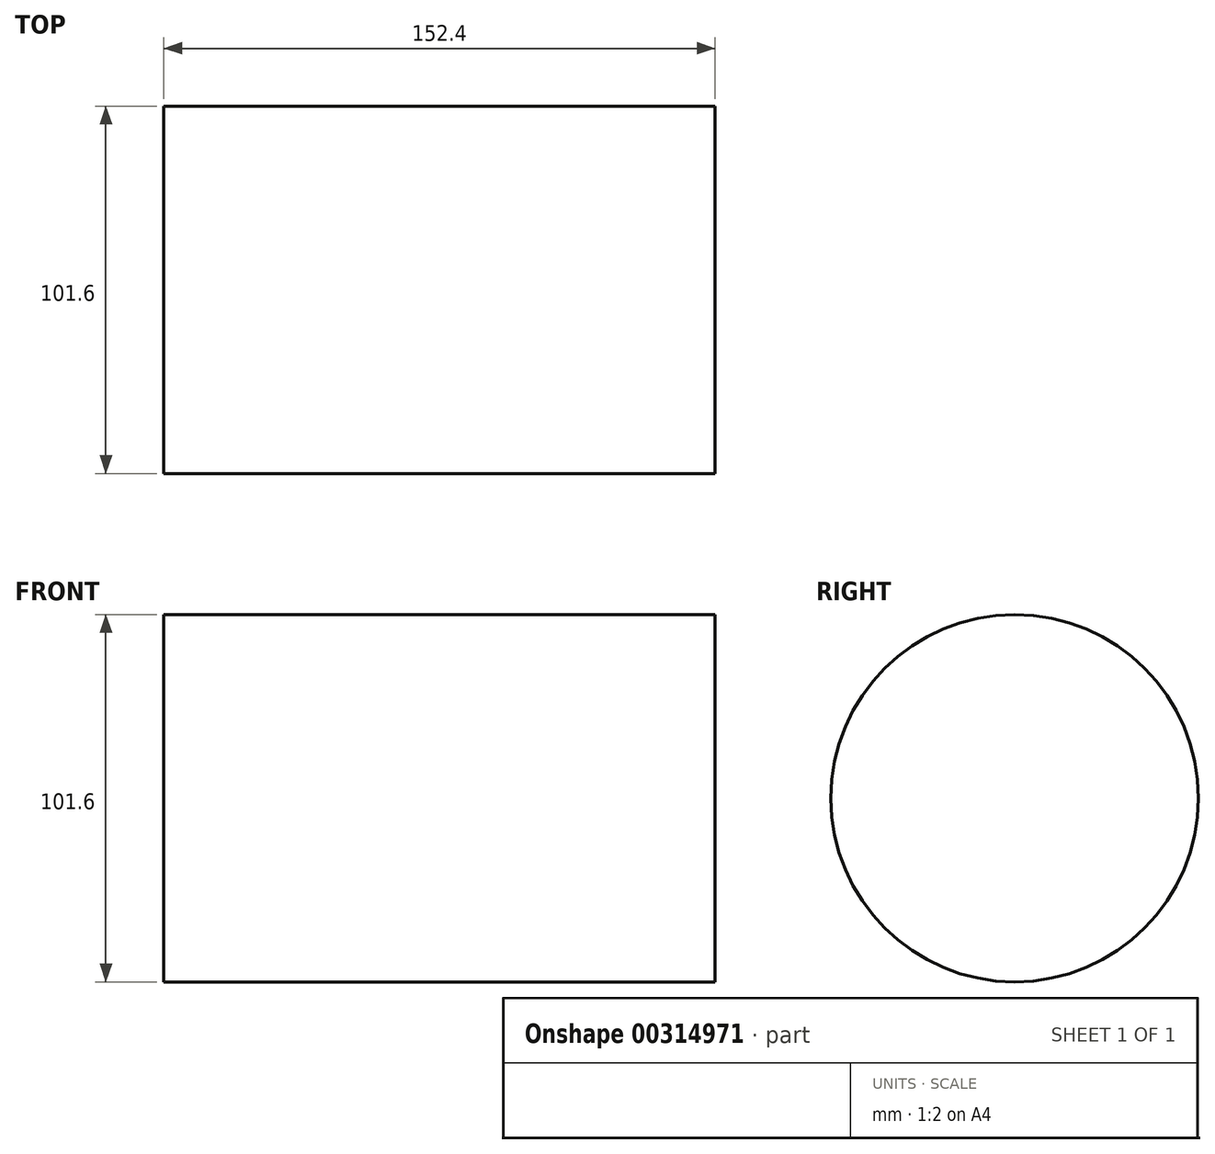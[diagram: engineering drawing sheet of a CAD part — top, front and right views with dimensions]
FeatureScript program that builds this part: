
annotation { "Feature Type Name" : "Feature", "Feature Type Description" : "" }
export const myFeature = defineFeature(function(context is Context, id is Id, definition is map)
    precondition{}
    {
        {
            var Q0;
            Q0=qCreatedBy(makeId("Right.planeOp"),FACE);
            var sketch = newSketch(context, id + "F0", { "sketchPlane" : qUnion([Q0])});
            skCircle(sketch, "E0", {"center": v(0, 0) * mm, "radius": 50.8 * mm});
            skSolve(sketch);
        }
        {
            var Q0;
            Q0 = qSketchRegion(id + "F0", true);
            extrude(context, id + "F1", {"entities" : qUnion([Q0]), "depth" : 152.4 * mm});
        }
    });
